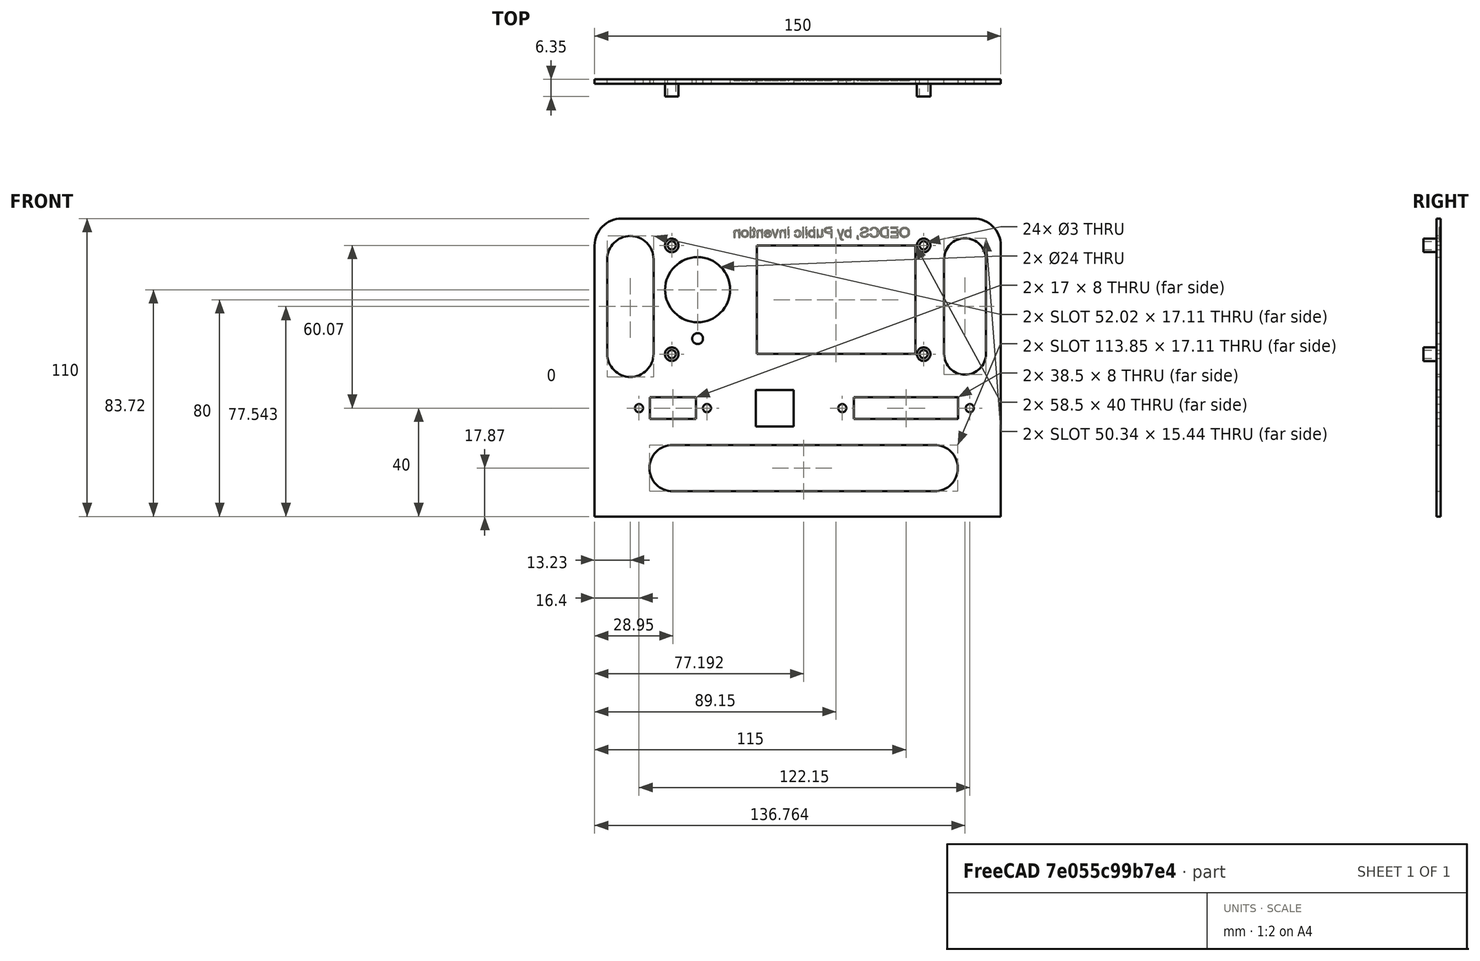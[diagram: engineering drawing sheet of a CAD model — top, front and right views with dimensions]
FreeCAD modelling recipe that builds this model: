
FCSTD DOCUMENT  (FreeCAD 0.19R24291 (Git))
Label: MountMini12864_b
License: All rights reserved
LicenseURL: http://en.wikipedia.org/wiki/All_rights_reserved
objects: TechDraw::DrawViewDimension×19, Sketcher::SketchObject×5, PartDesign::Pocket×3, PartDesign::Pad×2, Spreadsheet::Sheet×1, TechDraw::DrawSVGTemplate×1, PartDesign::Fillet×1, Part::Part2DObjectPython×1, PartDesign::Body×1, App::Part×1, TechDraw::DrawViewPart×1, TechDraw::DrawPage×1, Part::Extrusion×1, Part::Cut×1
note: 21 computed .brp shape members not serialized (recipe doc carries the construction recipe); baked Part::Feature solids carry a one-line shape summary decoded from their .brp

FEATURE [Sketcher::SketchObject] Sketch
  FullyConstrained = true
  MapMode = 5
  Placement = pos=(0,0,0) rot=(1,0,0;1.5708rad)
  Support = -> [XZ_Plane001]
  expr: Constraints[10] = <<Spreadsheet>>.Height
  expr: Constraints[9] = <<Spreadsheet>>.Width
  expr: Constraints[11] = <<Spreadsheet>>.OffsetVert
  expr: Constraints[12] = <<Spreadsheet>>.OffsetHorz
  sketch-geometry (5):
    g0: LineSegment StartX=-55 StartY=45 StartZ=0 EndX=95 EndY=45 EndZ=0
    g1: LineSegment StartX=95 StartY=45 StartZ=0 EndX=95 EndY=-65 EndZ=0
    g2: LineSegment StartX=95 StartY=-65 StartZ=0 EndX=-55 EndY=-65 EndZ=0
    g3: LineSegment StartX=-55 StartY=-65 StartZ=0 EndX=-55 EndY=45 EndZ=0
    g4: GeomPoint X=20 Y=-10 Z=0
  constraints (13):
    c: Coincident(g0,g1)
    c: Coincident(g1,g2)
    c: Coincident(g2,g3)
    c: Coincident(g3,g0)
    c: Horizontal(g0)
    c: Horizontal(g2)
    c: Vertical(g1)
    c: Vertical(g3)
    c: Symmetric(g0,g1,g4)
    c: DistanceX(g0,g0) = 150
    c: DistanceY(g3,g3) = 110
    c: DistanceY(g4,g-1) = 10
    c: DistanceX(g-1,g4) = 20
FEATURE [PartDesign::Pad] Pad  label="Pad Body"
  Direction = (1,1,1)
  Length = 1.5875
  Length2 = 100
  Placement = pos=(0,0,0) rot=(1,0,0;1.5708rad)
  Profile = -> Sketch
  Type = 0
  expr: Length = <<Spreadsheet>>.Thickness
FEATURE [Spreadsheet::Sheet] Spreadsheet
  cells = A1=MountMini12864; A2=Place a center point. Locate that point at Horz and Vertical Offset; A3=Place a rectangle around the point. ; A4=Select upper left corner, lower right cornder and center point. Set symetery; A5=Set Width to Width parameter (below), Set Height to Height Parameter below.; A6=Close the now fully parameterized and constrinaed sketch.; A7=Pad the sketch to the Depth prameter (below).; A9=Body; A10=OffsetHorz; B10(OffsetHorz)==20mm; A11=OffsetVert; B11(OffsetVert)==10mm; A13=Width; B13(Width)==150mm; C13=PCB is 189mm; A14=Height; B14(Height)==110mm; A15=Depth; B15(Depth)==3mm; A16=Thickness; B16(Thickness)==C16; C16==25.4 / 16; A18=DisplayMount; A19=OffsetMountHorz; B19(OffsetMountHorz)==20mm; C19=Toward left; A20=OffsetMountVert; B20(OffsetMountVert)==15mm; C21=From drawing; A22=DisplayMountWidth; B22(DisplayMountWidth)==C22; C22==101.99 - 8.99; A23=DisplayMountHeight; B23(DisplayMountHeight)==C23; C23==44 - 3.86; A24=DisplayMountHoleDiameter; B24(DisplayMountHoleDiameter)==3mm; A25=DisplayMountStandOffLength; B25(DisplayMountStandOffLength)==C25 * 25.4; C25=0.25; A27=OffsetDisplayHorz; B27(OffsetDisplayHorz)==61.6mm; C27=From edge; D27==70.59 - 8.99; A28=OffsetDisplayVert; B28(OffsetDisplayVert)==15mm; C28=From drawing; A29=DisplayWidth; B29(DisplayWidth)==58.5mm; C29==70.59 - 12.39; A30=DisplayHeight; B30(DisplayHeight)==40mm; C30==38.8mm; A32=OffsetEncoderHorz; B32(OffsetEncoderHorz)==12.53 - 3; C32=Guess; A33=OffserEncoderVert; B33(OffserEncoderVert)==(32.71 + 20.87) / 2 - 3; C33=Up from Mount; A34=EncoderDiameter; B34(EncoderDiameter)==24mm; C34=Measured Knob; A36=OffsetResetHorz; B36(OffsetResetHorz)==B32; C36=same as encoder; A37=OffserResetVert; B37(OffserResetVert)==5.75mm; C37=Up from Mount; A38=ResetDiameter; B38(ResetDiameter)==4mm; A41=DB25 Mount; A42=OffsetDB25MountHorz; B42(OffsetDB25MountHorz)==60mm; C42=This moves DB25, RJ12, and DB9; A43=OffsetDB25MountVert; B43(OffsetDB25MountVert)==25mm; C43=Down from center; A45=DB25MountWidth; B45(DB25MountWidth)==38.5mm; A46=DB25MountHeight; B46(DB25MountHeight)==8mm; A47=DB25MountHoleSpace; B47(DB25MountHoleSpace)==47.1mm; A48=DB25MountHoleDiameter; B48(DB25MountHoleDiameter)==3mm; A51=RJ12 Connector; A52=OffsetRJ12MountHorz; B52(OffsetRJ12MountHorz)==48.5mm; C52=From DB25; A53=OffsetRJ12MountVert; B53(OffsetRJ12MountVert)==25mm; A55=RJ12Width; B55(RJ12Width)==14mm; C55=13.5 mm measured; A56=RJ12Height; B56(RJ12Height)==13.5mm; C56=12.5 mm measured; A59=DB9 Mount; A60=OffsetDB9MountHorz; B60(OffsetDB9MountHorz)==86.05mm; A61=OffsetDB9MountVert; B61(OffsetDB9MountVert)==25mm; C61=Down from center; A63=DB9MountWidth; B63(DB9MountWidth)=17; C63==16.3mm; A64=DB9MountHeight; B64(DB9MountHeight)==8mm; A65=DB9MountHoleSpace; B65(DB9MountHoleSpace)==25.1mm; A66=DB9MountHoleDiameter; B66(DB9MountHoleDiameter)==3mm
FEATURE [Sketcher::SketchObject] Sketch001
  FullyConstrained = true
  MapMode = 5
  Placement = pos=(0,0,0) rot=(-1,0,0;1.5708rad)
  Support = -> [Pad]
  expr: Constraints[39] = <<Spreadsheet>>.OffsetMountHorz
  expr: Constraints[38] = <<Spreadsheet>>.OffsetEncoderHorz
  expr: Constraints[29] = <<Spreadsheet>>.DisplayWidth
  expr: Constraints[32] = <<Spreadsheet>>.OffsetDisplayHorz
  expr: Constraints[37] = <<Spreadsheet>>.OffserEncoderVert
  expr: Constraints[36] = <<Spreadsheet>>.OffserResetVert
  expr: Constraints[34] = <<Spreadsheet>>.ResetDiameter
  expr: Constraints[18] = <<Spreadsheet>>.DisplayMountHeight
  expr: Constraints[30] = <<Spreadsheet>>.DisplayHeight
  expr: Constraints[19] = <<Spreadsheet>>.OffsetMountVert
  expr: Constraints[33] = <<Spreadsheet>>.EncoderDiameter
  expr: Constraints[17] = <<Spreadsheet>>.DisplayMountWidth
  expr: Constraints[12] = <<Spreadsheet>>.DisplayMountHoleDiameter
  sketch-geometry (16):
    g0: LineSegment StartX=-26.5 StartY=5.07 StartZ=0 EndX=66.5 EndY=5.07 EndZ=0
    g1: LineSegment StartX=66.5 StartY=5.07 StartZ=0 EndX=66.5 EndY=-35.07 EndZ=0
    g2: LineSegment StartX=66.5 StartY=-35.07 StartZ=0 EndX=-26.5 EndY=-35.07 EndZ=0
    g3: LineSegment StartX=-26.5 StartY=-35.07 StartZ=0 EndX=-26.5 EndY=5.07 EndZ=0
    g4: GeomPoint X=20 Y=-15 Z=0
    g5: Circle CenterX=-26.5 CenterY=5.07 CenterZ=0 NormalX=0 NormalY=0 NormalZ=1 AngleXU=0 Radius=1.5
    g6: Circle CenterX=-26.5 CenterY=-35.07 CenterZ=0 NormalX=0 NormalY=0 NormalZ=1 AngleXU=0 Radius=1.5
    g7: Circle CenterX=66.5 CenterY=-35.07 CenterZ=0 NormalX=0 NormalY=0 NormalZ=1 AngleXU=0 Radius=1.5
    g8: Circle CenterX=66.5 CenterY=5.07 CenterZ=0 NormalX=0 NormalY=0 NormalZ=1 AngleXU=0 Radius=1.5
    g9: LineSegment StartX=4.9 StartY=5 StartZ=0 EndX=63.4 EndY=5 EndZ=0
    g10: LineSegment StartX=63.4 StartY=5 StartZ=0 EndX=63.4 EndY=-35 EndZ=0
    g11: LineSegment StartX=63.4 StartY=-35 StartZ=0 EndX=4.9 EndY=-35 EndZ=0
    g12: LineSegment StartX=4.9 StartY=-35 StartZ=0 EndX=4.9 EndY=5 EndZ=0
    g13: GeomPoint X=34.15 Y=-15 Z=0
    g14: Circle CenterX=-16.97 CenterY=-18.72 CenterZ=0 NormalX=0 NormalY=0 NormalZ=1 AngleXU=0 Radius=12
    g15: Circle CenterX=-16.97 CenterY=-0.68 CenterZ=0 NormalX=0 NormalY=0 NormalZ=1 AngleXU=0 Radius=2
  constraints (40):
    c: Coincident(g0,g1)
    c: Coincident(g1,g2)
    c: Coincident(g2,g3)
    c: Coincident(g3,g0)
    c: Horizontal(g0)
    c: Horizontal(g2)
    c: Vertical(g1)
    c: Vertical(g3)
    c: Symmetric(g0,g1,g4)
    c: Equal(g8,g7)
    c: Equal(g7,g6)
    c: Equal(g6,g5)
    c: Diameter(g5) = 3
    c: Coincident(g5,g0)
    c: Coincident(g6,g2)
    c: Coincident(g7,g1)
    c: Coincident(g8,g0)
    c: DistanceX(g0,g0) = 93
    c: DistanceY(g3,g3) = 40.14
    c: DistanceY(g4,g-1) = 15
    c: Coincident(g9,g10)
    c: Coincident(g10,g11)
    c: Coincident(g11,g12)
    c: Coincident(g12,g9)
    c: Horizontal(g9)
    c: Horizontal(g11)
    c: Vertical(g10)
    c: Vertical(g12)
    c: Symmetric(g9,g10,g13)
    c: DistanceX(g9,g9) = 58.5
    c: DistanceY(g10,g10) = 40
    c: Horizontal(g13,g4)
    c: DistanceX(g9,g8) = 61.6
    c: Diameter(g14) = 24
    c: Diameter(g15) = 4
    c: Vertical(g14,g15)
    c: DistanceY(g15,g5) = 5.75
    c: DistanceY(g14,g5) = 23.79
    c: DistanceX(g5,g14) = 9.53
    c: DistanceX(g-1,g4) = 20
FEATURE [PartDesign::Pocket] Pocket  label="PocketDisplayMountHoles"
  BaseFeature = -> Pad
  Length = 5
  Length2 = 100
  Placement = pos=(0,0,0) rot=(1,0,0;1.5708rad)
  Profile = -> Sketch001
  Type = 1
FEATURE [Sketcher::SketchObject] Sketch002
  FullyConstrained = true
  MapMode = 5
  Placement = pos=(0,0,0) rot=(-1,0,0;1.5708rad)
  Support = -> [Pocket]
  expr: Constraints[48] = <<Spreadsheet>>.DB9MountHoleSpace
  expr: Constraints[45] = <<Spreadsheet>>.OffsetDB9MountHorz
  expr: Constraints[42] = <<Spreadsheet>>.DB9MountWidth
  expr: Constraints[30] = <<Spreadsheet>>.RJ12Height
  expr: Constraints[32] = <<Spreadsheet>>.OffsetRJ12MountHorz
  expr: Constraints[29] = <<Spreadsheet>>.RJ12Width
  expr: Constraints[19] = <<Spreadsheet>>.OffsetDB25MountHorz
  expr: Constraints[43] = <<Spreadsheet>>.DB9MountHeight
  expr: Constraints[18] = <<Spreadsheet>>.DB25MountHoleSpace
  expr: Constraints[14] = <<Spreadsheet>>.DB25MountHoleDiameter
  expr: Constraints[9] = <<Spreadsheet>>.DB25MountWidth
  expr: Constraints[11] = <<Spreadsheet>>.OffsetDB25MountVert
  expr: Constraints[10] = <<Spreadsheet>>.DB25MountHeight
  sketch-geometry (21):
    g0: LineSegment StartX=40.75 StartY=29 StartZ=0 EndX=79.25 EndY=29 EndZ=0
    g1: LineSegment StartX=79.25 StartY=29 StartZ=0 EndX=79.25 EndY=21 EndZ=0
    g2: LineSegment StartX=79.25 StartY=21 StartZ=0 EndX=40.75 EndY=21 EndZ=0
    g3: LineSegment StartX=40.75 StartY=21 StartZ=0 EndX=40.75 EndY=29 EndZ=0
    g4: GeomPoint X=60 Y=25 Z=0
    g5: LineSegment StartX=36.45 StartY=25 StartZ=0 EndX=83.55 EndY=25 EndZ=0
    g6: Circle CenterX=36.45 CenterY=25 CenterZ=0 NormalX=0 NormalY=0 NormalZ=1 AngleXU=0 Radius=1.5
    g7: Circle CenterX=83.55 CenterY=25 CenterZ=0 NormalX=0 NormalY=0 NormalZ=1 AngleXU=0 Radius=1.5
    g8: LineSegment StartX=4.5 StartY=31.75 StartZ=0 EndX=18.5 EndY=31.75 EndZ=0
    g9: LineSegment StartX=18.5 StartY=31.75 StartZ=0 EndX=18.5 EndY=18.25 EndZ=0
    g10: LineSegment StartX=18.5 StartY=18.25 StartZ=0 EndX=4.5 EndY=18.25 EndZ=0
    g11: LineSegment StartX=4.5 StartY=18.25 StartZ=0 EndX=4.5 EndY=31.75 EndZ=0
    g12: GeomPoint X=11.5 Y=25 Z=0
    g13: LineSegment StartX=-34.55 StartY=29 StartZ=0 EndX=-17.55 EndY=29 EndZ=0
    g14: LineSegment StartX=-17.55 StartY=29 StartZ=0 EndX=-17.55 EndY=21 EndZ=0
    g15: LineSegment StartX=-17.55 StartY=21 StartZ=0 EndX=-34.55 EndY=21 EndZ=0
    g16: LineSegment StartX=-34.55 StartY=21 StartZ=0 EndX=-34.55 EndY=29 EndZ=0
    g17: GeomPoint X=-26.05 Y=25 Z=0
    g18: LineSegment StartX=-38.6 StartY=25 StartZ=0 EndX=-13.5 EndY=25 EndZ=0
    g19: Circle CenterX=-38.6 CenterY=25 CenterZ=0 NormalX=0 NormalY=0 NormalZ=1 AngleXU=0 Radius=1.5
    g20: Circle CenterX=-13.5 CenterY=25 CenterZ=0 NormalX=0 NormalY=0 NormalZ=1 AngleXU=0 Radius=1.5
  constraints (53):
    c: Coincident(g0,g1)
    c: Coincident(g1,g2)
    c: Coincident(g2,g3)
    c: Coincident(g3,g0)
    c: Horizontal(g0)
    c: Horizontal(g2)
    c: Vertical(g1)
    c: Vertical(g3)
    c: Symmetric(g0,g1,g4)
    c: DistanceX(g0,g0) = 38.5
    c: DistanceY(g3,g3) = 8
    c: DistanceY(g-1,g4) = 25
    c: Horizontal(g5)
    c: Symmetric(g5,g5,g4)
    c: Diameter(g6) = 3
    c: Equal(g6,g7)
    c: Coincident(g7,g5)
    c: Coincident(g6,g5)
    c: DistanceX(g5,g5) = 47.1
    c: DistanceX(g-1,g4) = 60
    c: Coincident(g8,g9)
    c: Coincident(g9,g10)
    c: Coincident(g10,g11)
    c: Coincident(g11,g8)
    c: Horizontal(g8)
    c: Horizontal(g10)
    c: Vertical(g9)
    c: Vertical(g11)
    c: Symmetric(g8,g9,g12)
    c: DistanceX(g8,g8) = 14
    c: DistanceY(g11,g11) = 13.5
    c: Horizontal(g12,g4)
    c: DistanceX(g12,g4) = 48.5
    c: Coincident(g13,g14)
    c: Coincident(g14,g15)
    c: Coincident(g15,g16)
    c: Coincident(g16,g13)
    c: Horizontal(g13)
    c: Horizontal(g15)
    c: Vertical(g14)
    c: Vertical(g16)
    c: Symmetric(g13,g14,g17)
    c: DistanceX(g13,g13) = 17
    c: DistanceY(g14,g14) = 8
    c: Horizontal(g17,g4)
    c: DistanceX(g17,g4) = 86.05
    c: Horizontal(g18)
    c: Symmetric(g18,g18,g17)
    c: DistanceX(g18,g18) = 25.1
    c: Equal(g19,g20)
    c: Equal(g20,g6)
    c: Coincident(g20,g18)
    c: Coincident(g19,g18)
FEATURE [PartDesign::Pocket] Pocket001  label="PockeDB25Mount"
  BaseFeature = -> Pocket
  Length = 5
  Length2 = 100
  Placement = pos=(0,0,0) rot=(1,0,0;1.5708rad)
  Profile = -> Sketch002
  Type = 1
FEATURE [TechDraw::DrawSVGTemplate] Template
  EditableTexts = Approved1=Approved 1; Approved2=Approved 2; CheckedBy=Checked By; Code=Code; CompanyAddress=1234 Main St; CompanyName=Company Name; DrawingNumber=Drawing Number; DrawingTitle1=Drawing Title 1; DrawingTitle2=Drawing Title 2; DrawingTitle3=Drawing Title 3; DrawnBy=Drawn By; Revision=Rev; Scale=Scale; Sheet=Sheet n of m
  Height = 215.9
  Orientation = 1
  Width = 279.4
FEATURE [Sketcher::SketchObject] Sketch003
  FullyConstrained = true
  MapMode = 5
  Placement = pos=(0,0,0) rot=(-1,0,0;1.5708rad)
  Support = -> [Pocket001]
  expr: Constraints[21] = <<Spreadsheet>>.DisplayMountHoleDiameter
  expr: Constraints[20] = <<Spreadsheet>>.OffsetDisplayVert
  expr: Constraints[19] = <<Spreadsheet>>.OffsetMountHorz
  expr: Constraints[18] = <<Spreadsheet>>.DisplayMountHeight
  expr: Constraints[17] = <<Spreadsheet>>.DisplayMountWidth
  sketch-geometry (13):
    g0: Circle CenterX=-26.5 CenterY=5.07 CenterZ=0 NormalX=0 NormalY=0 NormalZ=1 AngleXU=0 Radius=2.5
    g1: Circle CenterX=-26.5 CenterY=-35.07 CenterZ=0 NormalX=0 NormalY=0 NormalZ=1 AngleXU=0 Radius=2.5
    g2: Circle CenterX=66.5 CenterY=5.07 CenterZ=0 NormalX=0 NormalY=0 NormalZ=1 AngleXU=0 Radius=2.5
    g3: Circle CenterX=66.5 CenterY=-35.07 CenterZ=0 NormalX=0 NormalY=0 NormalZ=1 AngleXU=0 Radius=2.5
    g4: GeomPoint X=20 Y=-15 Z=0
    g5: LineSegment StartX=-26.5 StartY=5.07 StartZ=0 EndX=66.5 EndY=5.07 EndZ=0
    g6: LineSegment StartX=66.5 StartY=5.07 StartZ=0 EndX=66.5 EndY=-35.07 EndZ=0
    g7: LineSegment StartX=66.5 StartY=-35.07 StartZ=0 EndX=-26.5 EndY=-35.07 EndZ=0
    g8: LineSegment StartX=-26.5 StartY=-35.07 StartZ=0 EndX=-26.5 EndY=5.07 EndZ=0
    g9: Circle CenterX=-26.5 CenterY=5.07 CenterZ=0 NormalX=0 NormalY=0 NormalZ=1 AngleXU=0 Radius=1.5
    g10: Circle CenterX=-26.5 CenterY=-35.07 CenterZ=0 NormalX=0 NormalY=0 NormalZ=1 AngleXU=0 Radius=1.5
    g11: Circle CenterX=66.5 CenterY=5.07 CenterZ=0 NormalX=0 NormalY=0 NormalZ=1 AngleXU=0 Radius=1.5
    g12: Circle CenterX=66.5 CenterY=-35.07 CenterZ=0 NormalX=0 NormalY=0 NormalZ=1 AngleXU=0 Radius=1.5
  constraints (29):
    c: Diameter(g0) = 5
    c: Equal(g0,g2)
    c: Equal(g2,g1)
    c: Equal(g1,g3)
    c: Coincident(g5,g6)
    c: Coincident(g6,g7)
    c: Coincident(g7,g8)
    c: Coincident(g8,g5)
    c: Horizontal(g5)
    c: Horizontal(g7)
    c: Vertical(g6)
    c: Vertical(g8)
    c: Symmetric(g5,g6,g4)
    c: Coincident(g0,g5)
    c: Coincident(g1,g7)
    c: Coincident(g3,g6)
    c: Coincident(g2,g5)
    c: DistanceX(g5,g5) = 93
    c: DistanceY(g6,g6) = 40.14
    c: DistanceX(g-1,g4) = 20
    c: DistanceY(g4,g-1) = 15
    c: Diameter(g9) = 3
    c: Equal(g9,g10)
    c: Equal(g10,g12)
    c: Equal(g12,g11)
    c: Coincident(g9,g0)
    c: Coincident(g10,g1)
    c: Coincident(g3,g12)
    c: Coincident(g2,g11)
FEATURE [PartDesign::Pad] Pad001  label="Pad001MountStandoff"
  BaseFeature = -> Pocket001
  Direction = (1,1,1)
  Length = 6.35
  Length2 = 100
  Placement = pos=(0,0,0) rot=(1,0,0;1.5708rad)
  Profile = -> Sketch003
  Reversed = true
  Type = 0
  expr: Length = <<Spreadsheet>>.DisplayMountStandOffLength
FEATURE [Sketcher::SketchObject] Sketch004
  FullyConstrained = false
  MapMode = 5
  Placement = pos=(0,-1.5875,0) rot=(1,0,0;1.5708rad)
  Support = -> [Pad001]
  sketch-geometry (12):
    g0: ArcOfCircle CenterX=-26.1772 CenterY=-47.1305 CenterZ=0 NormalX=0 NormalY=0 NormalZ=1 AngleXU=0 Radius=8.555 StartAngle=1.5708 EndAngle=4.71239
    g1: ArcOfCircle CenterX=70.5609 CenterY=-47.1305 CenterZ=0 NormalX=0 NormalY=0 NormalZ=1 AngleXU=0 Radius=8.555 StartAngle=4.71239 EndAngle=7.85398
    g2: LineSegment StartX=-26.1772 StartY=-55.6855 StartZ=0 EndX=70.5609 EndY=-55.6855 EndZ=0
    g3: LineSegment StartX=-26.1772 StartY=-38.5755 StartZ=0 EndX=70.5609 EndY=-38.5755 EndZ=0
    g4: ArcOfCircle CenterX=-41.77 CenterY=29.9973 CenterZ=0 NormalX=0 NormalY=0 NormalZ=1 AngleXU=0 Radius=8.5548 StartAngle=1e-16 EndAngle=3.14159
    g5: ArcOfCircle CenterX=-41.77 CenterY=-4.91072 CenterZ=0 NormalX=0 NormalY=0 NormalZ=1 AngleXU=0 Radius=8.5548 StartAngle=3.14159 EndAngle=6.28319
    g6: LineSegment StartX=-50.3248 StartY=29.9973 StartZ=0 EndX=-50.3248 EndY=-4.91072 EndZ=0
    g7: LineSegment StartX=-33.2152 StartY=29.9973 StartZ=0 EndX=-33.2152 EndY=-4.91072 EndZ=0
    g8: ArcOfCircle CenterX=81.764 CenterY=29.9973 CenterZ=0 NormalX=0 NormalY=0 NormalZ=1 AngleXU=0 Radius=7.7185 StartAngle=2e-16 EndAngle=3.14159
    g9: ArcOfCircle CenterX=81.764 CenterY=-4.91072 CenterZ=0 NormalX=0 NormalY=0 NormalZ=1 AngleXU=0 Radius=7.7185 StartAngle=3.14159 EndAngle=6.28319
    g10: LineSegment StartX=74.0455 StartY=29.9973 StartZ=0 EndX=74.0455 EndY=-4.91072 EndZ=0
    g11: LineSegment StartX=89.4825 StartY=29.9973 StartZ=0 EndX=89.4825 EndY=-4.91072 EndZ=0
  constraints (25):
    c: Tangent(g0,g3) = 1.5708
    c: Tangent(g0,g2) = -1.5708
    c: Tangent(g2,g1) = -1.5708
    c: Tangent(g3,g1) = 1.5708
    c: Horizontal(g2)
    c: Equal(g0,g1)
    c: Tangent(g4,g7) = 1.5708
    c: Tangent(g4,g6) = -1.5708
    c: Tangent(g6,g5) = -1.5708
    c: Tangent(g7,g5) = 1.5708
    c: Vertical(g6)
    c: Equal(g4,g5)
    c: Tangent(g8,g11) = 1.5708
    c: Tangent(g8,g10) = -1.5708
    c: Tangent(g10,g9) = -1.5708
    c: Tangent(g11,g9) = 1.5708
    c: Vertical(g10)
    c: Equal(g8,g9)
    c: DistanceX(g4,g4) = 17.1096
    c: DistanceX(g8,g8) = 15.437
    c: Horizontal(g4,g8)
    c: Horizontal(g5,g9)
    c: DistanceX(g-1,g9) = 81.764
    c: DistanceX(g5,g9) = 123.534
    c: DistanceY(g0,g0) = 17.11
FEATURE [PartDesign::Pocket] Pocket002
  BaseFeature = -> Pad001
  Length = 5
  Length2 = 100
  Placement = pos=(0,0,0) rot=(1,0,0;1.5708rad)
  Profile = -> Sketch004
  Type = 1
FEATURE [PartDesign::Fillet] Fillet
  Base = -> Pocket002 [Edge2,Edge1]
  BaseFeature = -> Pocket002
  Placement = pos=(0,0,0) rot=(1,0,0;1.5708rad)
  Radius = 10
  SupportTransform = false
FEATURE [Part::Part2DObjectPython] ShapeString  # Draft 2D object (typed FeaturePython)
  FontFile = <path>
  Placement = pos=(61.4921,1,38) rot=(0,0.707107,0.707107;3.14159rad)
  Size = 4
  String = OEDCS, by Public Invention
  Support = -> [Pad]
  Tracking = 0
FEATURE [PartDesign::Body] Body  label="Body_MountMini12864"
  Group = -> [Sketch,Pad,Sketch001,Pocket,Sketch002,Pocket001,Sketch003,Pad001,Sketch004,Pocket002,Fillet,ShapeString]
  Origin = -> Origin001
  Tip = -> Fillet
FEATURE [App::Part] Part  label="Part_MountMini12864"
  Group = -> [Body]
  Origin = -> Origin
FEATURE [TechDraw::DrawViewPart] View
  CoarseView = false
  Direction = (0,1,0)
  Focus = 100
  HardHidden = false
  IsoCount = 0
  IsoHidden = false
  IsoVisible = false
  LockPosition = false
  Perspective = false
  Rotation = 0
  ScaleType = 2
  SeamHidden = false
  SeamVisible = true
  SmoothHidden = false
  SmoothVisible = true
  Source = -> [Part]
  X = 141.69
  XDirection = (-1,0,0)
  Y = 136.14
FEATURE [TechDraw::DrawViewDimension] Dimension
  Arbitrary = false
  ArbitraryTolerances = false
  EqualTolerance = true
  FormatSpec = %.3f
  FormatSpecOverTolerance = %+.3f
  FormatSpecUnderTolerance = %+.3f
  Inverted = false
  LockPosition = false
  MeasureType = 1
  OverTolerance = 0
  References2D = -> [View]
  Rotation = 0
  ScaleType = 2
  TheoreticalExact = false
  Type = 1
  UnderTolerance = 0
  X = -46.9351
  Y = 26.2363
FEATURE [TechDraw::DrawViewDimension] Dimension001
  Arbitrary = false
  ArbitraryTolerances = false
  EqualTolerance = true
  FormatSpec = %.3f
  FormatSpecOverTolerance = %+.3f
  FormatSpecUnderTolerance = %+.3f
  Inverted = false
  LockPosition = false
  MeasureType = 1
  OverTolerance = 0
  References2D = -> [View]
  Rotation = 0
  ScaleType = 2
  TheoreticalExact = false
  Type = 2
  UnderTolerance = 0
  X = -71.672
  Y = -29.179
FEATURE [TechDraw::DrawViewDimension] Dimension004
  Arbitrary = false
  ArbitraryTolerances = false
  EqualTolerance = true
  FormatSpec = ⌀%.3f
  FormatSpecOverTolerance = %+.3f
  FormatSpecUnderTolerance = %+.3f
  Inverted = false
  LockPosition = false
  MeasureType = 1
  OverTolerance = 0
  References2D = -> [View]
  Rotation = 0
  ScaleType = 2
  TheoreticalExact = false
  Type = 5
  UnderTolerance = 0
  X = 87.7226
  Y = 29.8842
FEATURE [TechDraw::DrawViewDimension] Dimension005
  Arbitrary = false
  ArbitraryTolerances = false
  EqualTolerance = true
  FormatSpec = ⌀%.3f
  FormatSpecOverTolerance = %+.3f
  FormatSpecUnderTolerance = %+.3f
  Inverted = false
  LockPosition = false
  MeasureType = 1
  OverTolerance = 0
  References2D = -> [View]
  Rotation = 0
  ScaleType = 2
  TheoreticalExact = false
  Type = 5
  UnderTolerance = 0
  X = 35.5581
  Y = -30.3195
FEATURE [TechDraw::DrawViewDimension] Dimension007
  Arbitrary = false
  ArbitraryTolerances = false
  EqualTolerance = true
  FormatSpec = %.3f
  FormatSpecOverTolerance = %+.3f
  FormatSpecUnderTolerance = %+.3f
  Inverted = false
  LockPosition = false
  MeasureType = 1
  OverTolerance = 0
  References2D = -> [View]
  Rotation = 0
  ScaleType = 2
  TheoreticalExact = false
  Type = 1
  UnderTolerance = 0
  X = -20.6064
  Y = 50.0465
FEATURE [TechDraw::DrawViewDimension] Dimension009
  Arbitrary = false
  ArbitraryTolerances = false
  EqualTolerance = true
  FormatSpec = %.3f
  FormatSpecOverTolerance = %+.3f
  FormatSpecUnderTolerance = %+.3f
  Inverted = false
  LockPosition = false
  MeasureType = 1
  OverTolerance = 0
  References2D = -> [View]
  Rotation = 0
  ScaleType = 2
  TheoreticalExact = false
  Type = 1
  UnderTolerance = 0
  X = 32.9041
  Y = 54.8532
FEATURE [TechDraw::DrawViewDimension] Dimension013
  Arbitrary = false
  ArbitraryTolerances = false
  EqualTolerance = true
  FormatSpec = %.3f
  FormatSpecOverTolerance = %+.3f
  FormatSpecUnderTolerance = %+.3f
  Inverted = false
  LockPosition = false
  MeasureType = 1
  OverTolerance = 0
  References2D = -> [View]
  Rotation = 0
  ScaleType = 2
  TheoreticalExact = false
  Type = 1
  UnderTolerance = 0
  X = 91.3994
  Y = -0.814891
FEATURE [TechDraw::DrawViewDimension] Dimension014
  Arbitrary = false
  ArbitraryTolerances = false
  EqualTolerance = true
  FormatSpec = %.3f
  FormatSpecOverTolerance = %+.3f
  FormatSpecUnderTolerance = %+.3f
  Inverted = false
  LockPosition = false
  MeasureType = 1
  OverTolerance = 0
  References2D = -> [View]
  Rotation = 0
  ScaleType = 2
  TheoreticalExact = false
  Type = 1
  UnderTolerance = 0
  X = 5.05625
  Y = -57.7938
FEATURE [TechDraw::DrawViewDimension] Dimension015
  Arbitrary = false
  ArbitraryTolerances = false
  EqualTolerance = true
  FormatSpec = %.3f
  FormatSpecOverTolerance = %+.3f
  FormatSpecUnderTolerance = %+.3f
  Inverted = false
  LockPosition = false
  MeasureType = 1
  OverTolerance = 0
  References2D = -> [View]
  Rotation = 0
  ScaleType = 2
  TheoreticalExact = false
  Type = 2
  UnderTolerance = 0
  X = -9.58058
  Y = -10.0272
FEATURE [TechDraw::DrawViewDimension] Dimension016
  Arbitrary = false
  ArbitraryTolerances = false
  EqualTolerance = true
  FormatSpec = %.3f
  FormatSpecOverTolerance = %+.3f
  FormatSpecUnderTolerance = %+.3f
  Inverted = false
  LockPosition = false
  MeasureType = 1
  OverTolerance = 0
  References2D = -> [View]
  Rotation = 0
  ScaleType = 2
  TheoreticalExact = false
  Type = 1
  UnderTolerance = 0
  X = -86.2432
  Y = -40.494
FEATURE [TechDraw::DrawViewDimension] Dimension017
  Arbitrary = false
  ArbitraryTolerances = false
  EqualTolerance = true
  FormatSpec = %.3f
  FormatSpecOverTolerance = %+.3f
  FormatSpecUnderTolerance = %+.3f
  Inverted = false
  LockPosition = false
  MeasureType = 1
  OverTolerance = 0
  References2D = -> [View]
  Rotation = 0
  ScaleType = 2
  TheoreticalExact = false
  Type = 1
  UnderTolerance = 0
  X = 99.8165
  Y = -7.76814
FEATURE [TechDraw::DrawViewDimension] Dimension018
  Arbitrary = false
  ArbitraryTolerances = false
  EqualTolerance = true
  FormatSpec = %.3f
  FormatSpecOverTolerance = %+.3f
  FormatSpecUnderTolerance = %+.3f
  Inverted = false
  LockPosition = false
  MeasureType = 1
  OverTolerance = 0
  References2D = -> [View]
  Rotation = 0
  ScaleType = 2
  TheoreticalExact = false
  Type = 1
  UnderTolerance = 0
  X = 82.2664
  Y = -55.464
FEATURE [TechDraw::DrawViewDimension] Dimension019
  Arbitrary = false
  ArbitraryTolerances = false
  EqualTolerance = true
  FormatSpec = %.3f
  FormatSpecOverTolerance = %+.3f
  FormatSpecUnderTolerance = %+.3f
  Inverted = false
  LockPosition = false
  MeasureType = 1
  OverTolerance = 0
  References2D = -> [View]
  Rotation = 0
  ScaleType = 2
  TheoreticalExact = false
  Type = 2
  UnderTolerance = 0
  X = 51.9089
  Y = -34.0732
FEATURE [TechDraw::DrawViewDimension] Dimension021
  Arbitrary = false
  ArbitraryTolerances = false
  EqualTolerance = true
  FormatSpec = %.3f
  FormatSpecOverTolerance = %+.3f
  FormatSpecUnderTolerance = %+.3f
  Inverted = false
  LockPosition = false
  MeasureType = 1
  OverTolerance = 0
  References2D = -> [View]
  Rotation = 0
  ScaleType = 2
  TheoreticalExact = false
  Type = 1
  UnderTolerance = 0
  X = -34.0152
  Y = 62.7763
FEATURE [TechDraw::DrawViewDimension] Dimension022
  Arbitrary = false
  ArbitraryTolerances = false
  EqualTolerance = true
  FormatSpec = %.3f
  FormatSpecOverTolerance = %+.3f
  FormatSpecUnderTolerance = %+.3f
  Inverted = false
  LockPosition = false
  MeasureType = 1
  OverTolerance = 0
  References2D = -> [View]
  Rotation = 0
  ScaleType = 2
  TheoreticalExact = false
  Type = 1
  UnderTolerance = 0
  X = -85.4324
  Y = 49.9656
FEATURE [TechDraw::DrawViewDimension] Dimension023
  Arbitrary = false
  ArbitraryTolerances = false
  EqualTolerance = true
  FormatSpec = %.3f
  FormatSpecOverTolerance = %+.3f
  FormatSpecUnderTolerance = %+.3f
  Inverted = false
  LockPosition = false
  MeasureType = 1
  OverTolerance = 0
  References2D = -> [View]
  Rotation = 0
  ScaleType = 2
  TheoreticalExact = false
  Type = 2
  UnderTolerance = 0
  X = 80.4755
  Y = -38.7945
FEATURE [TechDraw::DrawViewDimension] Dimension024
  Arbitrary = false
  ArbitraryTolerances = false
  EqualTolerance = true
  FormatSpec = %.3f
  FormatSpecOverTolerance = %+.3f
  FormatSpecUnderTolerance = %+.3f
  Inverted = false
  LockPosition = false
  MeasureType = 1
  OverTolerance = 0
  References2D = -> [View]
  Rotation = 0
  ScaleType = 2
  TheoreticalExact = false
  Type = 2
  UnderTolerance = 0
  X = -105.63
  Y = -25.5
FEATURE [TechDraw::DrawViewDimension] Dimension025
  Arbitrary = false
  ArbitraryTolerances = false
  EqualTolerance = true
  FormatSpec = %.3f
  FormatSpecOverTolerance = %+.3f
  FormatSpecUnderTolerance = %+.3f
  Inverted = false
  LockPosition = false
  MeasureType = 1
  OverTolerance = 0
  References2D = -> [View]
  Rotation = 0
  ScaleType = 2
  TheoreticalExact = false
  Type = 1
  UnderTolerance = 0
  X = -83.3792
  Y = 3.93382
FEATURE [TechDraw::DrawViewDimension] Dimension026
  Arbitrary = false
  ArbitraryTolerances = false
  EqualTolerance = true
  FormatSpec = %.3f
  FormatSpecOverTolerance = %+.3f
  FormatSpecUnderTolerance = %+.3f
  Inverted = false
  LockPosition = false
  MeasureType = 1
  OverTolerance = 0
  References2D = -> [View]
  Rotation = 0
  ScaleType = 2
  TheoreticalExact = false
  Type = 1
  UnderTolerance = 0
  X = -89.9939
  Y = -75.7733
FEATURE [TechDraw::DrawPage] Page
  KeepUpdated = true
  NextBalloonIndex = 1
  ProjectionType = 0
  Template = -> Template
  Views = -> [View,Dimension,Dimension001,Dimension004,Dimension005,Dimension007,Dimension009,Dimension013,Dimension014,Dimension015,Dimension016,Dimension017,Dimension018,Dimension019,Dimension021,Dimension022,Dimension023,Dimension024,Dimension025,Dimension026]
FEATURE [Part::Extrusion] Extrude
  Base = -> ShapeString
  Dir = (-4.37113e-08,1,-1e-15)
  DirMode = 2
  FaceMakerClass = Part::FaceMakerBullseye
  LengthFwd = -1.5
  LengthRev = 0
  Solid = true
  Symmetric = false
FEATURE [Part::Cut] Cut  label="Panel_CutWIthText"
  Base = -> Fillet
  Tool = -> Extrude
note: 1 file-system path scrubbed to <path> (originals preserved in the JSON sidecar)
